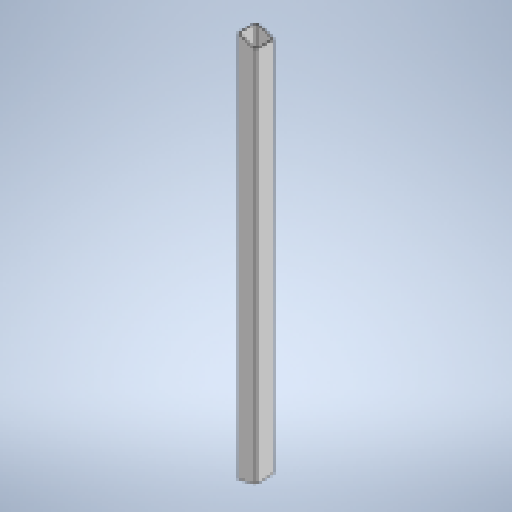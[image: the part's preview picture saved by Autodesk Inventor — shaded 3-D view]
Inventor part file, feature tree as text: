
AUTODESK INVENTOR PART (.ipt)
format: ipt  version: 2025 (Build 290162010, 162A)  size: 179,200 bytes
history: native  units: mm
features: extrude x2, sketch x2, mirror x1
ambient origin geometry x8: Origin, YZ Plane, XZ Plane, XY Plane, X Axis, Y Axis, Z Axis, Center Point
bodies: Solid1 (feature_tree)
feature tree (5):
  extrude  "Extrusion1"  Depth=8.0mm
  extrude  "Extrusion2"  Depth=120.0mm
  mirror  "Mirror1"
  sketch  "Sketch1"  dims[d0=8.0mm d1=120.0mm d2=120.0mm d3=4.0mm d6=8.0mm]
  sketch  "Sketch2"  dims[d7=120.0mm d8=120.0mm d9=4.0mm d14=2505.0mm d15=0.0mm d16=15.0deg d17=2000.0mm d18=0.0mm]
